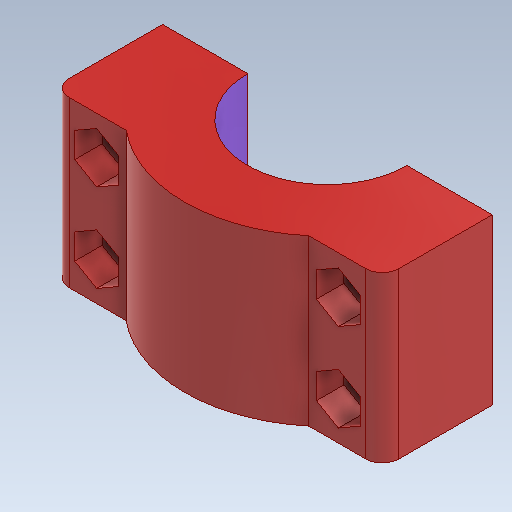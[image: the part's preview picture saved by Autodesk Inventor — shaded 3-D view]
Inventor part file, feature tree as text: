
AUTODESK INVENTOR PART (.ipt)
format: ipt  version: 2020.2 (Build 242310000, 310)  size: 247,296 bytes
history: native  units: mm
features: extrude x4, sketch x4, fillet x2, hole x1
ambient origin geometry x8: Origin, YZ Plane, XZ Plane, XY Plane, X Axis, Y Axis, Z Axis, Center Point
bodies: Solido1 (feature_tree)
feature tree (11):
  extrude  "Estrusione1"  Depth=20.0mm TaperAngle=0.0deg
  extrude  "Estrusione2"  Depth=30.0mm TaperAngle=0.0deg
  hole  "Foro3"  [1 undecoded]
  extrude  "Estrusione4"  Depth=60.0mm
  fillet  "Raccordo1"  Radius=7.0mm
  fillet  "Raccordo2"  Radius=22.0mm
  extrude  "Estrusione5"  TaperAngle=90.0deg  [1 undecoded]
  sketch  "Schizzo1"
  sketch  "Schizzo2"
  sketch  "Schizzo7"
  sketch  "Schizzo9"
note: 2 required parameter values undecoded (feature->parameter linkage not recoverable at this tier; creation-order binding heuristic only, values carry confidence <= 0.55)
